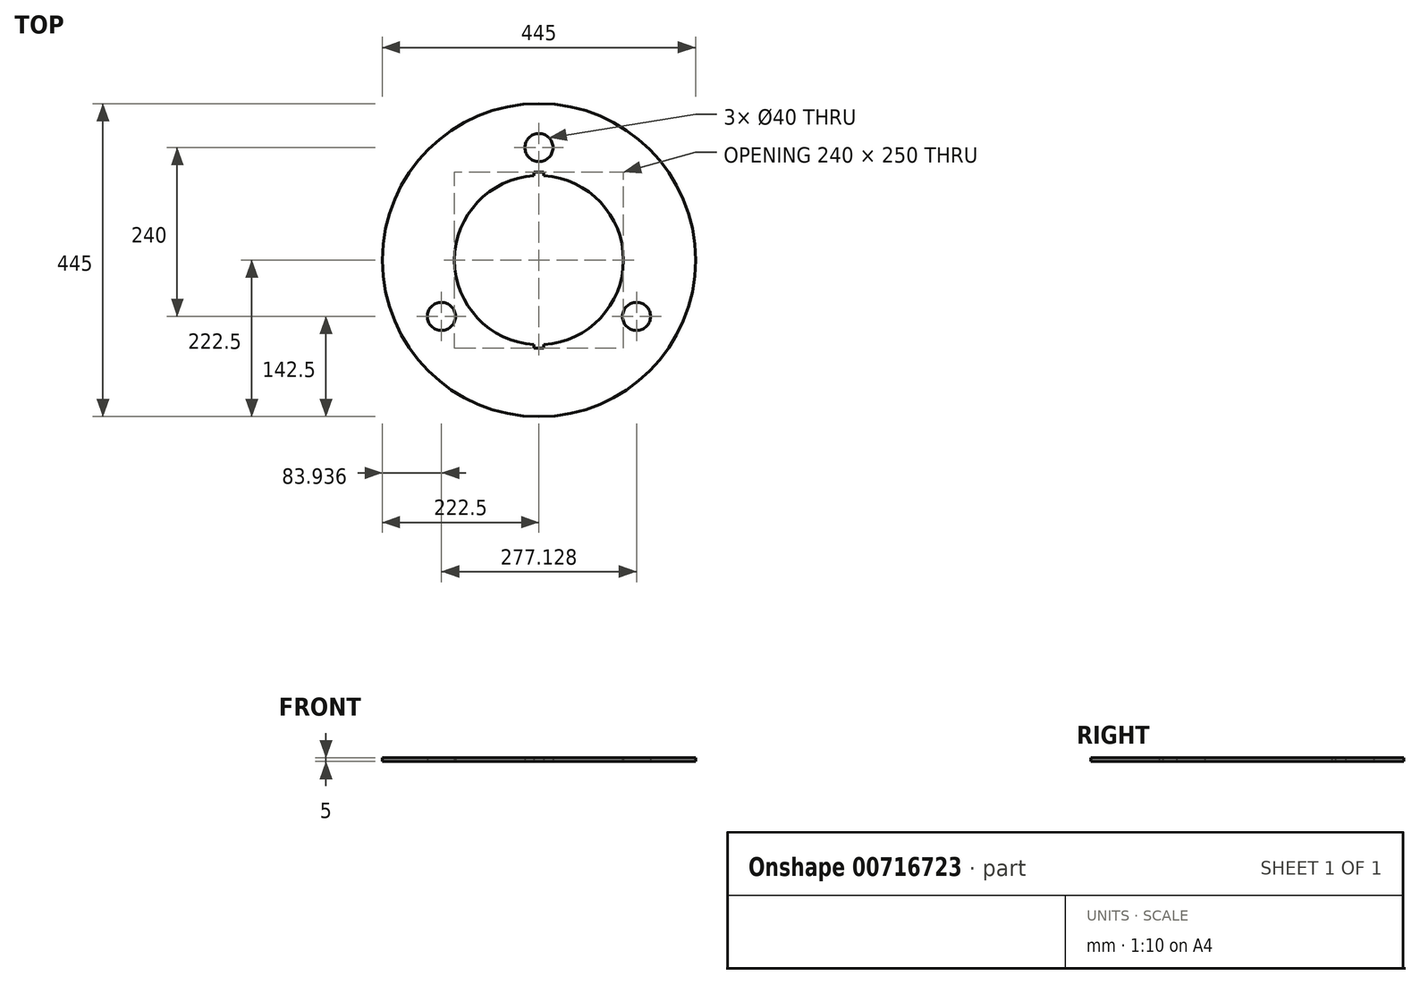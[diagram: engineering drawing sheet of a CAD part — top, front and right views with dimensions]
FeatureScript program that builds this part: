
annotation { "Feature Type Name" : "Feature", "Feature Type Description" : "" }
export const myFeature = defineFeature(function(context is Context, id is Id, definition is map)
    precondition{}
    {
        {
            var Q0;
            Q0=qCreatedBy(makeId("Top.planeOp"),FACE);
            var sketch = newSketch(context, id + "F0", { "sketchPlane" : qUnion([Q0])});
            skCircle(sketch, "E0", {"center": v(0, 0) * mm, "radius": 222.5 * mm});
            skCircle(sketch, "E1", {"center": v(0, 0) * mm, "radius": 120 * mm});
            skCircle(sketch, "E2", {"center": v(0, 160) * mm, "radius": 20 * mm});
            skCircle(sketch, "E3.1.0", {"center": v(-138.56, -80) * mm, "radius": 20 * mm});
            skCircle(sketch, "E3.2.0", {"center": v(138.56, -80) * mm, "radius": 20 * mm});
            skLineSegment(sketch, "E4.bottom", {"start": v(7, 115) * mm, "end": v(-7, 115) * mm});
            skLineSegment(sketch, "E4.top", {"start": v(7, 125) * mm, "end": v(-7, 125) * mm});
            skLineSegment(sketch, "E4.left", {"start": v(7, 115) * mm, "end": v(7, 125) * mm});
            skLineSegment(sketch, "E4.right", {"start": v(-7, 115) * mm, "end": v(-7, 125) * mm});
            skPoint(sketch, "E4.middle", {"position": v(0, 120) * mm});
            skLineSegment(sketch, "E5.1.0", {"start": v(-7, -115) * mm, "end": v(-7, -125) * mm});
            skLineSegment(sketch, "E5.1.1", {"start": v(7, -115) * mm, "end": v(7, -125) * mm});
            skPoint(sketch, "E5.1.2", {"position": v(0, -120) * mm});
            skLineSegment(sketch, "E5.1.3", {"start": v(-7, -125) * mm, "end": v(7, -125) * mm});
            skLineSegment(sketch, "E5.1.4", {"start": v(-7, -115) * mm, "end": v(7, -115) * mm});
            skSolve(sketch);
        }
        {
            var Q0;
            Q0=makeQuery(id+"F0.imprint","IMPRINT",FACE,{"disambiguationData":[TD([[makeQuery(id+"F0.imprint","IMPRINT",EDGE,{"derivedFrom":sQuery(id+"F0.wireOp",EDGE,"E0")}),1.0]])]});
            extrude(context, id + "F1", {"entities" : qUnion([Q0]), "depth" : 5 * mm, "offsetDistance" : 25 * mm});
        }
    });
